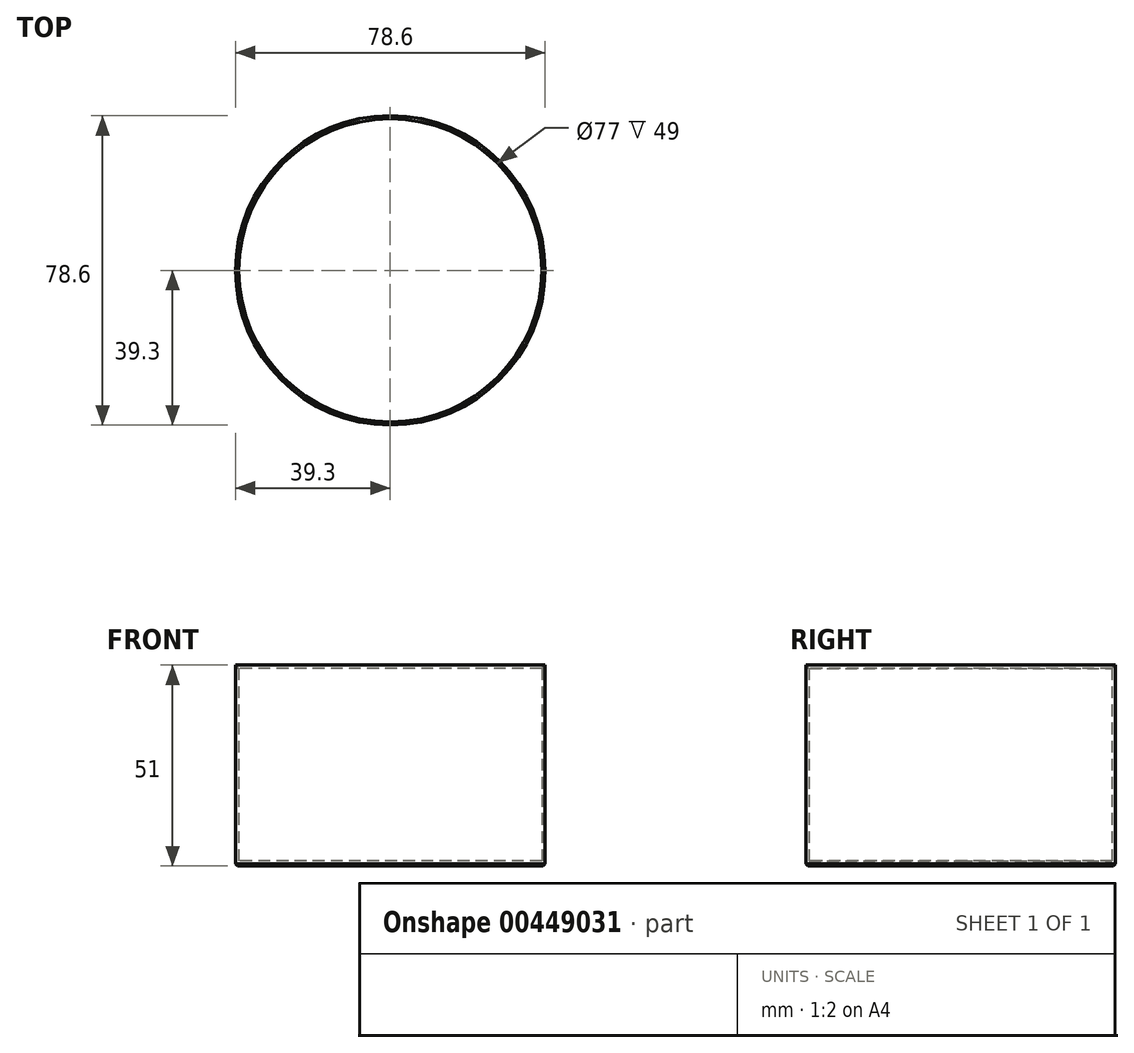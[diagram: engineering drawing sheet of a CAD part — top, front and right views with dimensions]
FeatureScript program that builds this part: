
annotation { "Feature Type Name" : "Feature", "Feature Type Description" : "" }
export const myFeature = defineFeature(function(context is Context, id is Id, definition is map)
    precondition{}
    {
        {
            var Q0;
            Q0=qCreatedBy(makeId("Top.planeOp"),FACE);
            var sketch = newSketch(context, id + "F0", { "sketchPlane" : qUnion([Q0])});
            skCircle(sketch, "E0", {"center": v(0, 0) * mm, "radius": 38.5 * mm});
            skCircle(sketch, "E1", {"center": v(0, 0) * mm, "radius": 39.3 * mm});
            skSolve(sketch);
        }
        {
            var Q0;
            Q0=makeQuery(id+"F0.imprint","IMPRINT",FACE,{"disambiguationData":[TD([[makeQuery(id+"F0.imprint","IMPRINT",EDGE,{"derivedFrom":sQuery(id+"F0.wireOp",EDGE,"E0")}),-1.0]])]});
            var Q1;
            Q1=makeQuery(id+"F0.imprint","IMPRINT",FACE,{"disambiguationData":[TD([[makeQuery(id+"F0.imprint","IMPRINT",EDGE,{"derivedFrom":sQuery(id+"F0.wireOp",EDGE,"E0")}),1.0]])]});
            extrude(context, id + "F1", {"entities" : qUnion([Q0, Q1]), "oppositeDirection" : true, "depth" : 1.2 * mm});
        }
        {
            var Q0;
            Q0 = qSketchRegion(id + "F0", true);
            extrude(context, id + "F2", {"entities" : qUnion([Q0]), "operationType" : NewBodyOperationType.ADD, "depth" : 50 * mm});
        }
        {
            var Q0;
            Q0=makeQuery(id+"F2.opExtrude","CAP_EDGE",EDGE,{"disambiguationData":[OSD([sQuery(id+"F0.wireOp",EDGE,"E0")])],"isStart":false});
            chamfer(context, id + "F3", {"entities" : qUnion([Q0]), "width" : 1 * mm, "tangentPropagation" : true});
        }
        {
            var Q0;
            Q0=makeQuery(id+"F1.opExtrude","CAP_EDGE",EDGE,{"disambiguationData":[OSD([sQuery(id+"F0.wireOp",EDGE,"E1")])],"isStart":false});
            chamfer(context, id + "F4", {"entities" : qUnion([Q0]), "width" : 0.5 * mm, "tangentPropagation" : true});
        }
    });
